# Revit family: ROTADO_РотационныйДефлектор_TST
name_source: partatom
category: Воздухораспределители
units: mm (PartAtom-declared; Revit-internal decimal feet)

## family parameters
Всегда вертикально = Да
На основе рабочей плоскости = Нет
Общий = Нет
При загрузке вырезать с полостями = Нет
Размер круглого соединителя = Использовать диаметр
Тип детали = Нормальный
Точка расчета площади = Нет

## types (7) — shared parameters
ADSK_URL документации изделия = https://rotado.ru
ADSK_URL страницы изделия = https://rotado.ru
ADSK_Версия Revit = 2019
ADSK_Единица измерения = шт.
ADSK_Завод-изготовитель = ROTADO
ADSK_Количество = 1
ADSK_Материал = ROTADO_Сталь_Нержавеющая_Оцинкованная
ADSK_Наименование = Ротационный дефлектор
URL = https://rotado.ru
Изготовитель = ROTADO
Описание = Вентиляционное вытяжное устройство, предназначенное для защиты воздуховодов и усиления тяги.
Производитель_Контакты_Телефон = 88007002460

## per-type parameters (varying)
| type | ADSK_Марка | ADSK_Масса | ADSK_Масса_Текст | ADSK_Обозначение | ADSK_Размер_Высота | ADSK_Размер_Диаметр | ADSK_Размер_Длина | ADSK_Размер_Ширина | D | D_1 | H | h | Высота_ламель |
| TST-315 | ROTADO TST-315 | 3 | 3 | ROTADO TST-315 | 370 мм | 315 мм | 440 мм | 440 мм | 317 мм | 440 мм | 370 мм | 100 мм | 228 мм |
| TST-355 | ROTADO TST-355 | 3.2 | 3.2 | ROTADO TST-355 | 450 мм | 355 мм | 500 мм | 500 мм | 357 мм | 500 мм | 450 мм | 100 мм | 308 мм |
| TST-400 | ROTADO TST-400 | 4 | 4 | ROTADO TST-400 | 530 мм | 400 мм | 550 мм | 550 мм | 402 мм | 550 мм | 530 мм | 200 мм | 288 мм |
| TST-500 | ROTADO TST-500 | 5 | 5 | ROTADO TST-500 | 530 мм | 500 мм | 600 мм | 600 мм | 502 мм | 600 мм | 530 мм | 200 мм | 288 мм |
| TST-600 | ROTADO TST-600 | 7 | 7 | ROTADO TST-600 | 600 мм | 600 мм | 800 мм | 800 мм | 602 мм | 800 мм | 600 мм | 250 мм | 308 мм |
| TST-680 | ROTADO TST-680 | 9 | 9 | ROTADO TST-680 | 600 мм | 680 мм | 800 мм | 800 мм | 682 мм | 800 мм | 600 мм | 250 мм | 308 мм |
| TST-800 | ROTADO TST-800 | 11 | 11 | ROTADO TST-800 | 600 мм | 800 мм | 900 мм | 900 мм | 802 мм | 900 мм | 600 мм | 250 мм | 308 мм |
